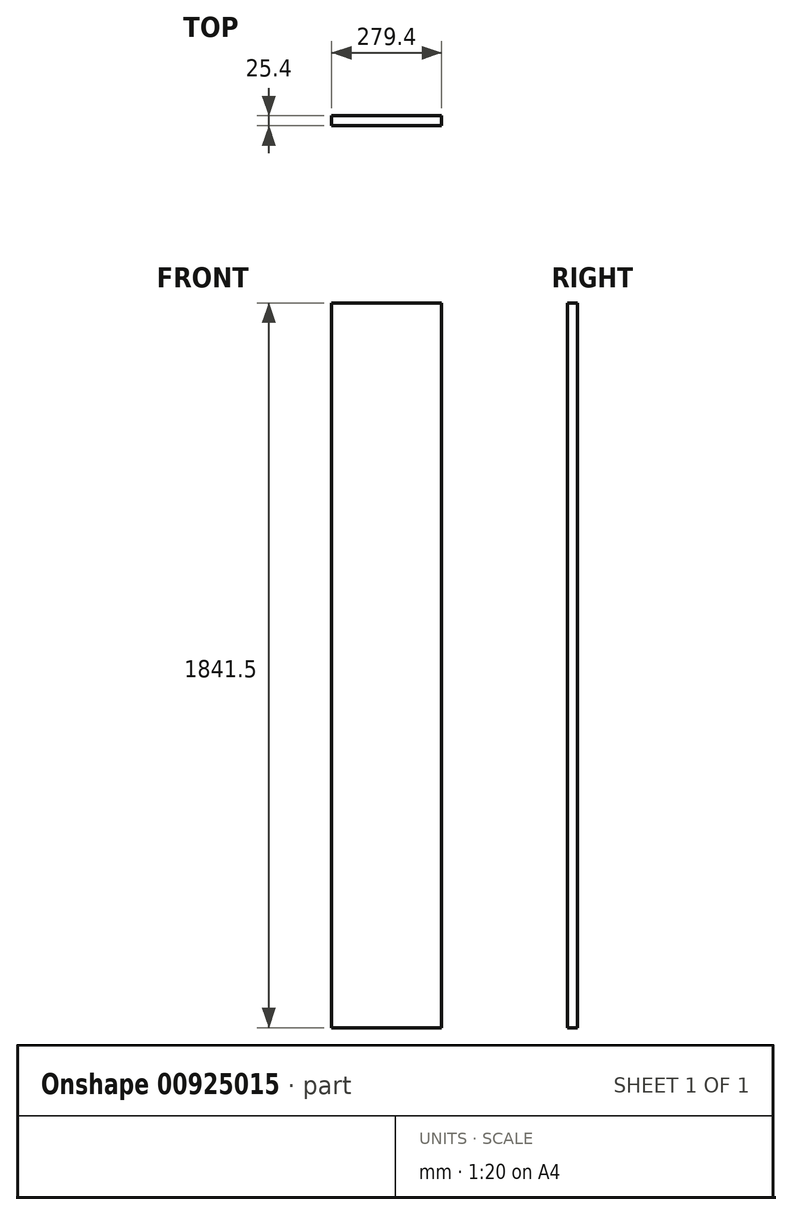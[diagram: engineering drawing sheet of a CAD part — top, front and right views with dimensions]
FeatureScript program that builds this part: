
annotation { "Feature Type Name" : "Feature", "Feature Type Description" : "" }
export const myFeature = defineFeature(function(context is Context, id is Id, definition is map)
    precondition{}
    {
        {
            var Q0;
            Q0=qCreatedBy(makeId("Front.planeOp"),FACE);
            var sketch = newSketch(context, id + "F0", { "sketchPlane" : qUnion([Q0])});
            skLineSegment(sketch, "E0.bottom", {"start": v(-279.4, 1841.5) * mm, "end": v(0, 1841.5) * mm});
            skLineSegment(sketch, "E0.top", {"start": v(-279.4, 0) * mm, "end": v(0, 0) * mm});
            skLineSegment(sketch, "E0.left", {"start": v(-279.4, 1841.5) * mm, "end": v(-279.4, 0) * mm});
            skLineSegment(sketch, "E0.right", {"start": v(0, 1841.5) * mm, "end": v(0, 0) * mm});
            skSolve(sketch);
        }
        {
            var Q0;
            Q0=makeQuery(id+"F0.imprint","IMPRINT",FACE,{"disambiguationData":[TD([[makeQuery(id+"F0.imprint","IMPRINT",EDGE,{"derivedFrom":sQuery(id+"F0.wireOp",EDGE,"E0.bottom")}),-1.0]])]});
            extrude(context, id + "F1", {"entities" : qUnion([Q0]), "depth" : 25.4 * mm, "offsetDistance" : 25.4 * mm});
        }
    });
